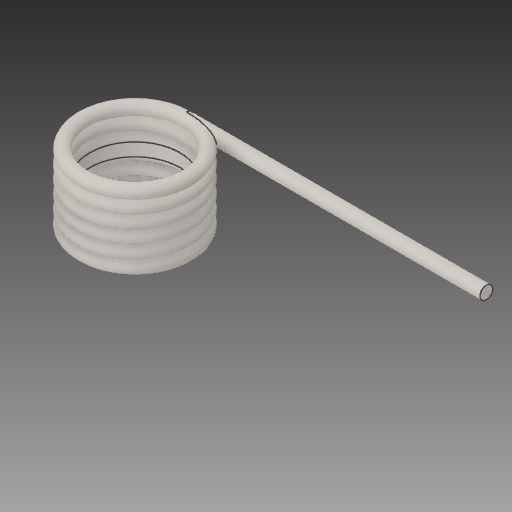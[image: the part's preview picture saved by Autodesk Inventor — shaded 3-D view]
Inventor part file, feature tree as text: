
AUTODESK INVENTOR PART (.ipt)
format: ipt  version: 2018 (Build 220112000, 112)  size: 312,832 bytes
history: native  units: mm
features: other x6, revolve x4
ambient origin geometry x8: Origin, YZ Plane, XZ Plane, XY Plane, X Axis, Y Axis, Z Axis, Center Point
bodies: Body1 (feature_tree), Body2 (feature_tree), Body3 (feature_tree), Body4 (feature_tree), Body5 (feature_tree)
feature tree (10):
  other  "ソリッド1"
  other  "ソリッド2"
  other  "ソリッド3"
  other  "ソリッド4"
  other  "ソリッド5"
  revolve  "Revolve1[2]"  [1 undecoded]
  revolve  "Revolve1[3]"  [1 undecoded]
  revolve  "Revolve1[4]"  [1 undecoded]
  revolve  "Revolve1[5]"  [1 undecoded]
  other  "Boss-Extrude1"
note: 4 required parameter values undecoded (feature->parameter linkage not recoverable at this tier; creation-order binding heuristic only, values carry confidence <= 0.55)
